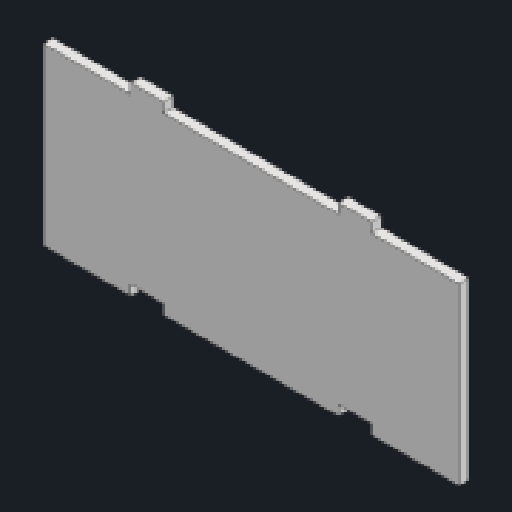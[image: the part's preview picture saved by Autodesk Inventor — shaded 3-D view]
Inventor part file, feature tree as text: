
AUTODESK INVENTOR PART (.ipt)
format: ipt  version: 2023 (Build 270158000, 158)  size: 206,848 bytes
history: native  units: mm
features: reference x21, other x6, extrude x5, sketch x5
ambient origin geometry x8: Origin, YZ Plane, XZ Plane, XY Plane, X Axis, Y Axis, Z Axis, Center Point
bodies: Solid1 (feature_tree)
feature tree (37):
  extrude  "Extrusion1"  Depth=50.0mm
  extrude  "Extrusion2"  Depth=3.0mm TaperAngle=0.0deg
  extrude  "Extrusion5"  Depth=10.0mm
  extrude  "Extrusion6"  Depth=10.0mm
  extrude  "Extrusion7"  Depth=10.0mm
  sketch  "Sketch1"  dims[d0=120.0mm d1=50.0mm]
  sketch  "Sketch2"  dims[d2=3.0mm d3=0.0mm d4=3.0mm d5=0.0mm]
  reference  "Reference1"
  reference  "Reference2"
  reference  "Reference3"
  reference  "Reference4"
  reference  "Reference5"
  reference  "Reference6"
  reference  "Reference7"
  reference  "Reference8"
  reference  "Reference9"
  reference  "Reference10"
  reference  "Reference11"
  reference  "Reference12"
  reference  "Reference13"
  reference  "Reference14"
  reference  "Reference15"
  reference  "Reference16"
  reference  "Reference17"
  reference  "Reference18"
  reference  "Reference19"
  sketch  "Sketch4"  dims[d10=126.0mm d11=31.5mm d18=10.0mm]
  sketch  "Sketch5"  dims[d19=3.0mm d20=10.0mm d21=3.0mm]
  reference  "Reference20"
  sketch  "Sketch6"  dims[d22=126.0mm d23=31.5mm d24=31.5mm d25=3.0mm d26=0.0mm d27=3.0mm d28=0.0mm d29=23.0mm d30=3.0mm d31=10.0mm d32=23.0mm d33=3.0mm d34=10.0mm d35=0.0mm d36=0.0mm d37=0.5mm d38=0.872665mm]
  reference  "Reference21"
  parser-record x1  (decoder bookkeeping rows leaked as tree rows — omitted from the tree; the rows remain in map.json)
  other  "AlarmClock.iam"
  other  "Bottom:1"
  other  "left:1"
  other  "right:1"
  other  "top:1"
note: 1 file-system path scrubbed to <path> (originals preserved in map.json)
